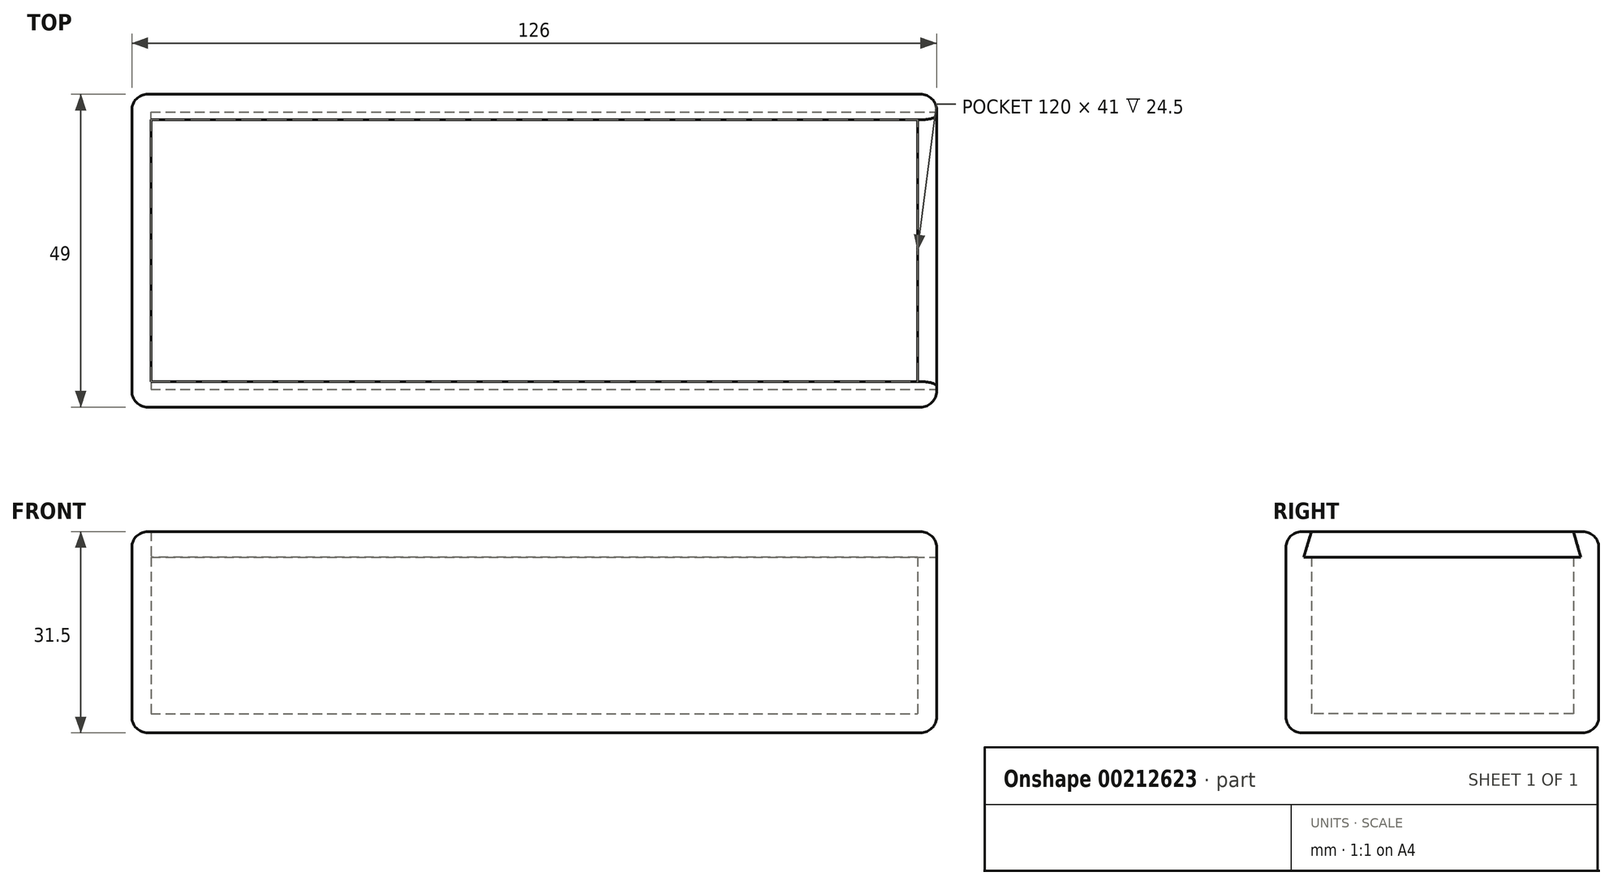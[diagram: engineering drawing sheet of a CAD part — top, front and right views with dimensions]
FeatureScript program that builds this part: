
annotation { "Feature Type Name" : "Feature", "Feature Type Description" : "" }
export const myFeature = defineFeature(function(context is Context, id is Id, definition is map)
    precondition{}
    {
        {
            assignVariable(context, id + "F0", {"name" : "mag", "anyValue" : 25.5});
        }
        {
            var Q0;
            Q0=qCreatedBy(makeId("Top.planeOp"),FACE);
            var sketch = newSketch(context, id + "F1", { "sketchPlane" : qUnion([Q0])});
            skLineSegment(sketch, "E0.bottom", {"start": v(-62.87, 16.22) * mm, "end": v(63.13, 16.22) * mm});
            skLineSegment(sketch, "E0.top", {"start": v(-62.87, -32.78) * mm, "end": v(63.13, -32.78) * mm});
            skLineSegment(sketch, "E0.left", {"start": v(-62.87, 16.22) * mm, "end": v(-62.87, -32.78) * mm});
            skLineSegment(sketch, "E0.right", {"start": v(63.13, 16.22) * mm, "end": v(63.13, -32.78) * mm});
            skLineSegment(sketch, "E1.bottom", {"start": v(-59.87, 12.22) * mm, "end": v(60.13, 12.22) * mm});
            skLineSegment(sketch, "E1.top", {"start": v(-59.87, -28.78) * mm, "end": v(60.13, -28.78) * mm});
            skLineSegment(sketch, "E1.left", {"start": v(-59.87, 12.22) * mm, "end": v(-59.87, -28.78) * mm});
            skLineSegment(sketch, "E1.right", {"start": v(60.13, 12.22) * mm, "end": v(60.13, -28.78) * mm});
            skSolve(sketch);
        }
        {
            var Q0;
            Q0=makeQuery(id+"F1.imprint","IMPRINT",FACE,{"disambiguationData":[TD([[makeQuery(id+"F1.imprint","IMPRINT",EDGE,{"derivedFrom":sQuery(id+"F1.wireOp",EDGE,"E0.bottom")}),-1.0]])]});
            var Q1;
            Q1=makeQuery(id+"F1.imprint","IMPRINT",FACE,{"disambiguationData":[TD([[makeQuery(id+"F1.imprint","IMPRINT",EDGE,{"derivedFrom":sQuery(id+"F1.wireOp",EDGE,"E1.bottom")}),-1.0]])]});
            extrude(context, id + "F2", {"entities" : qUnion([Q0, Q1]), "oppositeDirection" : true, "depth" : 3 * mm});
        }
        {
            var Q0;
            Q0=makeQuery(id+"F1.imprint","IMPRINT",FACE,{"disambiguationData":[TD([[makeQuery(id+"F1.imprint","IMPRINT",EDGE,{"derivedFrom":sQuery(id+"F1.wireOp",EDGE,"E0.bottom")}),-1.0]])]});
            extrude(context, id + "F3", {"entities" : qUnion([Q0]), "operationType" : NewBodyOperationType.ADD, "depth" : (getVariable(context, 'mag') + 3) * mm, "offsetDistance" : 25 * mm});
        }
        {
            var Q0;
            {var subQ0=sQuery(id+"F1.wireOp",EDGE,"E0.right");Q0=makeQuery(id+"F3.boolean.opBoolean","MERGE",FACE,{"derivedFrom":[makeQuery(id+"F2.opExtrude","SWEPT_FACE",FACE,{"disambiguationData":[OSD([subQ0])]}),makeQuery(id+"F3.opExtrude","SWEPT_FACE",FACE,{"disambiguationData":[OSD([subQ0])]})]});}
            var sketch = newSketch(context, id + "F4", { "sketchPlane" : qUnion([Q0])});
            skLineSegment(sketch, "E2.bottom", {"start": v(-28.78, 28.5) * mm, "end": v(12.22, 28.5) * mm});
            skLineSegment(sketch, "E2.top", {"start": v(-28.78, 24.5) * mm, "end": v(12.22, 24.5) * mm});
            skLineSegment(sketch, "E3", {"start": v(-28.78, 28.5) * mm, "end": v(-29.98, 24.5) * mm});
            skLineSegment(sketch, "E4", {"start": v(-29.98, 24.5) * mm, "end": v(-28.78, 24.5) * mm});
            skLineSegment(sketch, "E5", {"start": v(12.22, 28.5) * mm, "end": v(13.42, 24.5) * mm});
            skLineSegment(sketch, "E6", {"start": v(13.42, 24.5) * mm, "end": v(12.22, 24.5) * mm});
            skSolve(sketch);
        }
        {
            var Q0;
            Q0=makeQuery(id+"F4.imprint","IMPRINT",FACE,{"disambiguationData":[TD([[makeQuery(id+"F4.imprint","IMPRINT",EDGE,{"derivedFrom":sQuery(id+"F4.wireOp",EDGE,"E2.bottom")}),1.0]])]});
            extrude(context, id + "F5", {"entities" : qUnion([Q0]), "operationType" : NewBodyOperationType.REMOVE, "oppositeDirection" : true, "depth" : 123 * mm});
        }
        {
            var Q0;
            {var subQ0=sQuery(id+"F1.wireOp",EDGE,"E0.right");var subQ1=sQuery(id+"F1.wireOp",EDGE,"E0.top");Q0=makeQuery(id+"F3.boolean.opBoolean","MERGE",EDGE,{"derivedFrom":[makeQuery(id+"F2.opExtrude","SWEPT_EDGE",EDGE,{"disambiguationData":[OSD([subQ1,subQ0])]}),makeQuery(id+"F3.opExtrude","SWEPT_EDGE",EDGE,{"disambiguationData":[OSD([subQ1,subQ0])]})]});}
            var Q1;
            {var subQ0=sQuery(id+"F1.wireOp",EDGE,"E0.right");var subQ1=sQuery(id+"F1.wireOp",EDGE,"E0.bottom");Q1=makeQuery(id+"F3.boolean.opBoolean","MERGE",EDGE,{"derivedFrom":[makeQuery(id+"F2.opExtrude","SWEPT_EDGE",EDGE,{"disambiguationData":[OSD([subQ1,subQ0])]}),makeQuery(id+"F3.opExtrude","SWEPT_EDGE",EDGE,{"disambiguationData":[OSD([subQ1,subQ0])]})]});}
            var Q2;
            {var subQ0=sQuery(id+"F1.wireOp",EDGE,"E0.left");var subQ1=sQuery(id+"F1.wireOp",EDGE,"E0.top");Q2=makeQuery(id+"F3.boolean.opBoolean","MERGE",EDGE,{"derivedFrom":[makeQuery(id+"F2.opExtrude","SWEPT_EDGE",EDGE,{"disambiguationData":[OSD([subQ1,subQ0])]}),makeQuery(id+"F3.opExtrude","SWEPT_EDGE",EDGE,{"disambiguationData":[OSD([subQ1,subQ0])]})]});}
            var Q3;
            {var subQ0=sQuery(id+"F1.wireOp",EDGE,"E0.left");var subQ1=sQuery(id+"F1.wireOp",EDGE,"E0.bottom");Q3=makeQuery(id+"F3.boolean.opBoolean","MERGE",EDGE,{"derivedFrom":[makeQuery(id+"F2.opExtrude","SWEPT_EDGE",EDGE,{"disambiguationData":[OSD([subQ1,subQ0])]}),makeQuery(id+"F3.opExtrude","SWEPT_EDGE",EDGE,{"disambiguationData":[OSD([subQ1,subQ0])]})]});}
            var Q4;
            Q4=makeQuery(id+"F2.opExtrude","CAP_EDGE",EDGE,{"disambiguationData":[OSD([sQuery(id+"F1.wireOp",EDGE,"E0.bottom")])],"isStart":false});
            var Q5;
            Q5=makeQuery(id+"F2.opExtrude","CAP_EDGE",EDGE,{"disambiguationData":[OSD([sQuery(id+"F1.wireOp",EDGE,"E0.right")])],"isStart":false});
            var Q6;
            Q6=makeQuery(id+"F2.opExtrude","CAP_EDGE",EDGE,{"disambiguationData":[OSD([sQuery(id+"F1.wireOp",EDGE,"E0.top")])],"isStart":false});
            var Q7;
            Q7=makeQuery(id+"F2.opExtrude","CAP_EDGE",EDGE,{"disambiguationData":[OSD([sQuery(id+"F1.wireOp",EDGE,"E0.left")])],"isStart":false});
            var Q8;
            Q8=makeQuery(id+"F3.opExtrude","CAP_EDGE",EDGE,{"disambiguationData":[OSD([sQuery(id+"F1.wireOp",EDGE,"E0.top")])],"isStart":false});
            var Q9;
            Q9=makeQuery(id+"F3.opExtrude","CAP_EDGE",EDGE,{"disambiguationData":[OSD([sQuery(id+"F1.wireOp",EDGE,"E0.left")])],"isStart":false});
            var Q10;
            Q10=makeQuery(id+"F3.opExtrude","CAP_EDGE",EDGE,{"disambiguationData":[OSD([sQuery(id+"F1.wireOp",EDGE,"E0.bottom")])],"isStart":false});
            var Q11;
            {var subQ0=sQuery(id+"F1.wireOp",EDGE,"E0.right");var subQ1=sQuery(id+"F1.wireOp",EDGE,"E0.bottom");Q11=makeQuery(id+"F5.boolean.opBoolean","SPLIT",EDGE,{"disambiguationData":[TD([makeQuery(id+"F2.opExtrude","SWEPT_FACE",FACE,{"disambiguationData":[OSD([subQ1])]})])],"derivedFrom":makeQuery(id+"F3.opExtrude","CAP_EDGE",EDGE,{"disambiguationData":[OSD([subQ0])],"isStart":false})});}
            var Q12;
            {var subQ0=sQuery(id+"F1.wireOp",EDGE,"E0.top");var subQ1=sQuery(id+"F1.wireOp",EDGE,"E0.right");Q12=makeQuery(id+"F5.boolean.opBoolean","SPLIT",EDGE,{"disambiguationData":[TD([makeQuery(id+"F2.opExtrude","SWEPT_FACE",FACE,{"disambiguationData":[OSD([subQ0])]})])],"derivedFrom":makeQuery(id+"F3.opExtrude","CAP_EDGE",EDGE,{"disambiguationData":[OSD([subQ1])],"isStart":false})});}
            fillet(context, id + "F6", {"entities" : qUnion([Q0, Q1, Q2, Q3, Q4, Q5, Q6, Q7, Q8, Q9, Q10, Q11, Q12]), "radius" : 2.5 * mm, "tangentPropagation" : true, "allowEdgeOverflow" : false});
        }
    });
